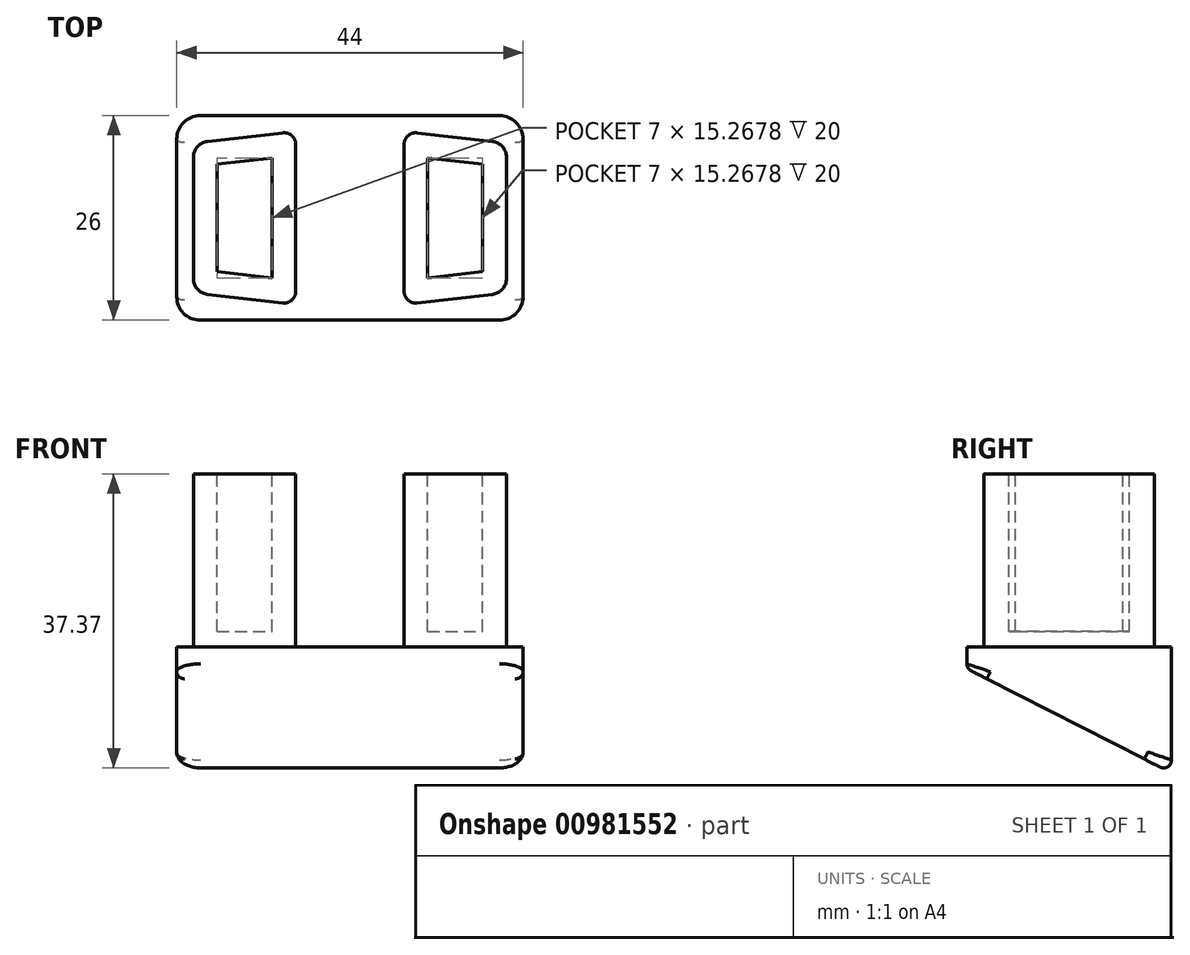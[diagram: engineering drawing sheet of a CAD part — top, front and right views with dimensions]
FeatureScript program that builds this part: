
annotation { "Feature Type Name" : "Feature", "Feature Type Description" : "" }
export const myFeature = defineFeature(function(context is Context, id is Id, definition is map)
    precondition{}
    {
        {
            var Q0;
            Q0=qCreatedBy(makeId("Top.planeOp"),FACE);
            var sketch = newSketch(context, id + "F0", { "sketchPlane" : qUnion([Q0])});
            skLineSegment(sketch, "E0.bottom", {"start": v(22, -13) * mm, "end": v(-22, -13) * mm});
            skLineSegment(sketch, "E0.top", {"start": v(22, 13) * mm, "end": v(-22, 13) * mm});
            skLineSegment(sketch, "E0.left", {"start": v(22, -13) * mm, "end": v(22, 13) * mm});
            skLineSegment(sketch, "E0.right", {"start": v(-22, -13) * mm, "end": v(-22, 13) * mm});
            skPoint(sketch, "E0.middle", {"position": v(0, 0) * mm});
            skSolve(sketch);
        }
        {
            var Q0;
            Q0=qSketchRegion(id+"F0",true);
            extrude(context, id + "F1", {"entities" : qUnion([Q0]), "flatOperationType" : FlatOperationType.REMOVE, "depth" : 16 * mm, "offsetDistance" : 25 * mm, "domain" : OperationDomain.MODEL});
        }
        {
            var Q0;
            Q0=makeQuery(id+"F1.opExtrude","CAP_FACE",FACE,{"disambiguationData":[OSD([sQuery(id+"F0.wireOp",EDGE,"E0.bottom"),sQuery(id+"F0.wireOp",EDGE,"E0.top"),sQuery(id+"F0.wireOp",EDGE,"E0.left"),sQuery(id+"F0.wireOp",EDGE,"E0.right")])],"isStart":false});
            var sketch = newSketch(context, id + "F2", { "sketchPlane" : qUnion([Q0]), "disableImprinting" : false});
            skPoint(sketch, "E1.0", {"position": v(0, 0) * mm});
            skLineSegment(sketch, "E2", {"start": v(6.88, -9.32) * mm, "end": v(6.88, 9.32) * mm});
            skLineSegment(sketch, "E3", {"start": v(8.55, 10.8) * mm, "end": v(18.1, 9.7) * mm});
            skLineSegment(sketch, "E4", {"start": v(19.88, 7.72) * mm, "end": v(19.88, -7.72) * mm});
            skLineSegment(sketch, "E5", {"start": v(18.1, -9.7) * mm, "end": v(8.55, -10.8) * mm});
            skLineSegment(sketch, "E6", {"start": v(0, 0) * mm, "end": v(22, 0) * mm, "construction": true});
            skPoint(sketch, "E7.visualSharp", {"position": v(19.88, 9.5) * mm});
            skArc(sketch, "E7.filletArc", {"start": v(19.88, 7.72) * mm, "mid": v(19.37, 9.05) * mm, "end": v(18.1, 9.7) * mm});
            skPoint(sketch, "E8.visualSharp", {"position": v(19.88, -9.5) * mm});
            skArc(sketch, "E8.filletArc", {"start": v(18.1, -9.7) * mm, "mid": v(19.37, -9.05) * mm, "end": v(19.88, -7.72) * mm});
            skLineSegment(sketch, "E9.MirrorCS", {"start": v(-6.88, -9.32) * mm, "end": v(-6.88, 9.32) * mm});
            skLineSegment(sketch, "E10.MirrorCS", {"start": v(-8.55, 10.8) * mm, "end": v(-18.1, 9.7) * mm});
            skLineSegment(sketch, "E11.MirrorCS", {"start": v(-19.88, 7.72) * mm, "end": v(-19.88, -7.72) * mm});
            skLineSegment(sketch, "E12.MirrorCS", {"start": v(-18.1, -9.7) * mm, "end": v(-8.55, -10.8) * mm});
            skArc(sketch, "E13.MirrorCS", {"start": v(-19.88, 7.72) * mm, "mid": v(-19.37, 9.05) * mm, "end": v(-18.1, 9.7) * mm});
            skPoint(sketch, "E14.MirrorP", {"position": v(-19.88, 9.5) * mm});
            skArc(sketch, "E15.MirrorCS", {"start": v(-18.1, -9.7) * mm, "mid": v(-19.37, -9.05) * mm, "end": v(-19.88, -7.72) * mm});
            skPoint(sketch, "E16.MirrorP", {"position": v(-19.88, -9.5) * mm});
            skPoint(sketch, "E17.0.visualSharp", {"position": v(-6.88, 11) * mm});
            skArc(sketch, "E17.0.filletArc", {"start": v(-6.88, 9.32) * mm, "mid": v(-7.38, 10.44) * mm, "end": v(-8.55, 10.8) * mm});
            skPoint(sketch, "E18.0.visualSharp", {"position": v(-6.88, -11) * mm});
            skArc(sketch, "E18.0.filletArc", {"start": v(-8.55, -10.8) * mm, "mid": v(-7.38, -10.44) * mm, "end": v(-6.88, -9.32) * mm});
            skPoint(sketch, "E19.0.visualSharp", {"position": v(6.88, -11) * mm});
            skArc(sketch, "E19.0.filletArc", {"start": v(6.88, -9.32) * mm, "mid": v(7.38, -10.44) * mm, "end": v(8.55, -10.8) * mm});
            skPoint(sketch, "E20.0.visualSharp", {"position": v(6.88, 11) * mm});
            skArc(sketch, "E20.0.filletArc", {"start": v(8.55, 10.8) * mm, "mid": v(7.38, 10.44) * mm, "end": v(6.88, 9.32) * mm});
            skSolve(sketch);
        }
        {
            var Q0;
            Q0=qSketchRegion(id+"F2",true);
            var Q1;
            Q1=makeQuery(id+"F2.imprint","IMPRINT",FACE,{"disambiguationData":[TD([[makeQuery(id+"F2.imprint","IMPRINT",EDGE,{"derivedFrom":sQuery(id+"F2.wireOp",EDGE,"E2")}),-1.0]])]});
            extrude(context, id + "F3", {"entities" : qUnion([Q0, Q1]), "operationType" : NewBodyOperationType.ADD, "depth" : 22 * mm, "offsetDistance" : 25 * mm});
        }
        {
            var Q0;
            Q0=makeQuery(id+"F1.opExtrude","SWEPT_EDGE",EDGE,{"disambiguationData":[OSD([sQuery(id+"F0.wireOp",EDGE,"E0.top"),sQuery(id+"F0.wireOp",EDGE,"E0.left")])]});
            var Q1;
            Q1=makeQuery(id+"F1.opExtrude","SWEPT_EDGE",EDGE,{"disambiguationData":[OSD([sQuery(id+"F0.wireOp",EDGE,"E0.top"),sQuery(id+"F0.wireOp",EDGE,"E0.right")])]});
            var Q2;
            Q2=makeQuery(id+"F1.opExtrude","SWEPT_EDGE",EDGE,{"disambiguationData":[OSD([sQuery(id+"F0.wireOp",EDGE,"E0.bottom"),sQuery(id+"F0.wireOp",EDGE,"E0.left")])]});
            var Q3;
            Q3=makeQuery(id+"F1.opExtrude","SWEPT_EDGE",EDGE,{"disambiguationData":[OSD([sQuery(id+"F0.wireOp",EDGE,"E0.bottom"),sQuery(id+"F0.wireOp",EDGE,"E0.right")])]});
            fillet(context, id + "F4", {"entities" : qUnion([Q0, Q1, Q2, Q3]), "radius" : 3 * mm, "tangentPropagation" : true, "allowEdgeOverflow" : false});
        }
        {
            var Q0;
            Q0=makeQuery(id+"F3.opExtrude","CAP_FACE",FACE,{"disambiguationData":[OSD([sQuery(id+"F2.wireOp",EDGE,"E2"),sQuery(id+"F2.wireOp",EDGE,"E3"),sQuery(id+"F2.wireOp",EDGE,"E4"),sQuery(id+"F2.wireOp",EDGE,"E5"),sQuery(id+"F2.wireOp",EDGE,"E7.filletArc"),sQuery(id+"F2.wireOp",EDGE,"E8.filletArc")])],"isStart":false});
            var sketch = newSketch(context, id + "F5", { "sketchPlane" : qUnion([Q0]), "disableImprinting" : false});
            skLineSegment(sketch, "E21.0", {"start": v(16.88, -6.83) * mm, "end": v(16.88, 6.83) * mm});
            skLineSegment(sketch, "E21.1", {"start": v(9.87, -7.63) * mm, "end": v(16.88, -6.83) * mm});
            skLineSegment(sketch, "E21.2", {"start": v(9.87, 7.63) * mm, "end": v(9.87, -7.63) * mm});
            skLineSegment(sketch, "E21.3", {"start": v(16.88, 6.83) * mm, "end": v(9.87, 7.63) * mm});
            skPoint(sketch, "E22.0", {"position": v(0, 0) * mm});
            skLineSegment(sketch, "E23.MirrorCS", {"start": v(-16.88, 6.83) * mm, "end": v(-9.87, 7.63) * mm});
            skLineSegment(sketch, "E24.MirrorCS", {"start": v(-9.87, 7.63) * mm, "end": v(-9.87, -7.63) * mm});
            skLineSegment(sketch, "E25.MirrorCS", {"start": v(-9.87, -7.63) * mm, "end": v(-16.88, -6.83) * mm});
            skLineSegment(sketch, "E26.MirrorCS", {"start": v(-16.88, -6.83) * mm, "end": v(-16.88, 6.83) * mm});
            skSolve(sketch);
        }
        {
            var Q0;
            Q0=makeQuery(id+"F5.imprint","IMPRINT",FACE,{"disambiguationData":[TD([[makeQuery(id+"F5.imprint","IMPRINT",EDGE,{"derivedFrom":sQuery(id+"F5.wireOp",EDGE,"E23.MirrorCS")}),-1.0]])]});
            var Q1;
            Q1=makeQuery(id+"F5.imprint","IMPRINT",FACE,{"disambiguationData":[TD([[makeQuery(id+"F5.imprint","IMPRINT",EDGE,{"derivedFrom":sQuery(id+"F5.wireOp",EDGE,"E21.0")}),1.0]])]});
            extrude(context, id + "F6", {"entities" : qUnion([Q0, Q1]), "operationType" : NewBodyOperationType.REMOVE, "oppositeDirection" : true, "depth" : 20 * mm, "offsetDistance" : 25 * mm});
        }
        {
            var Q0;
            Q0=makeQuery(id+"F1.opExtrude","SWEPT_FACE",FACE,{"disambiguationData":[OSD([sQuery(id+"F0.wireOp",EDGE,"E0.left")])]});
            var sketch = newSketch(context, id + "F7", { "sketchPlane" : qUnion([Q0]), "disableImprinting" : false});
            skLineSegment(sketch, "E27", {"start": v(13, 0) * mm, "end": v(-13, 13.25) * mm});
            skLineSegment(sketch, "E28", {"start": v(-13, 13.25) * mm, "end": v(-13, 0) * mm});
            skLineSegment(sketch, "E29", {"start": v(-13, 0) * mm, "end": v(13, 0) * mm});
            skSolve(sketch);
        }
        {
            var Q0;
            Q0 = qSketchRegion(id + "F7", true);
            extrude(context, id + "F8", {"entities" : qUnion([Q0]), "operationType" : NewBodyOperationType.REMOVE, "oppositeDirection" : true, "depth" : 44 * mm, "offsetDistance" : 25 * mm});
        }
        {
            var Q0;
            Q0=makeQuery(id+"F8.boolean.opBoolean","MERGE",EDGE,{"derivedFrom":[makeQuery(id+"F1.opExtrude","CAP_EDGE",EDGE,{"disambiguationData":[OSD([sQuery(id+"F0.wireOp",EDGE,"E0.top")])],"isStart":true})],"fromTools":[makeQuery(id+"F8.opExtrude","SWEPT_EDGE",EDGE,{"disambiguationData":[OSD([sQuery(id+"F7.wireOp",EDGE,"E27"),sQuery(id+"F7.wireOp",EDGE,"E29")])]})]});
            fillet(context, id + "F9", {"entities" : qUnion([Q0]), "radius" : 1 * mm, "tangentPropagation" : true, "allowEdgeOverflow" : false});
        }
    });
